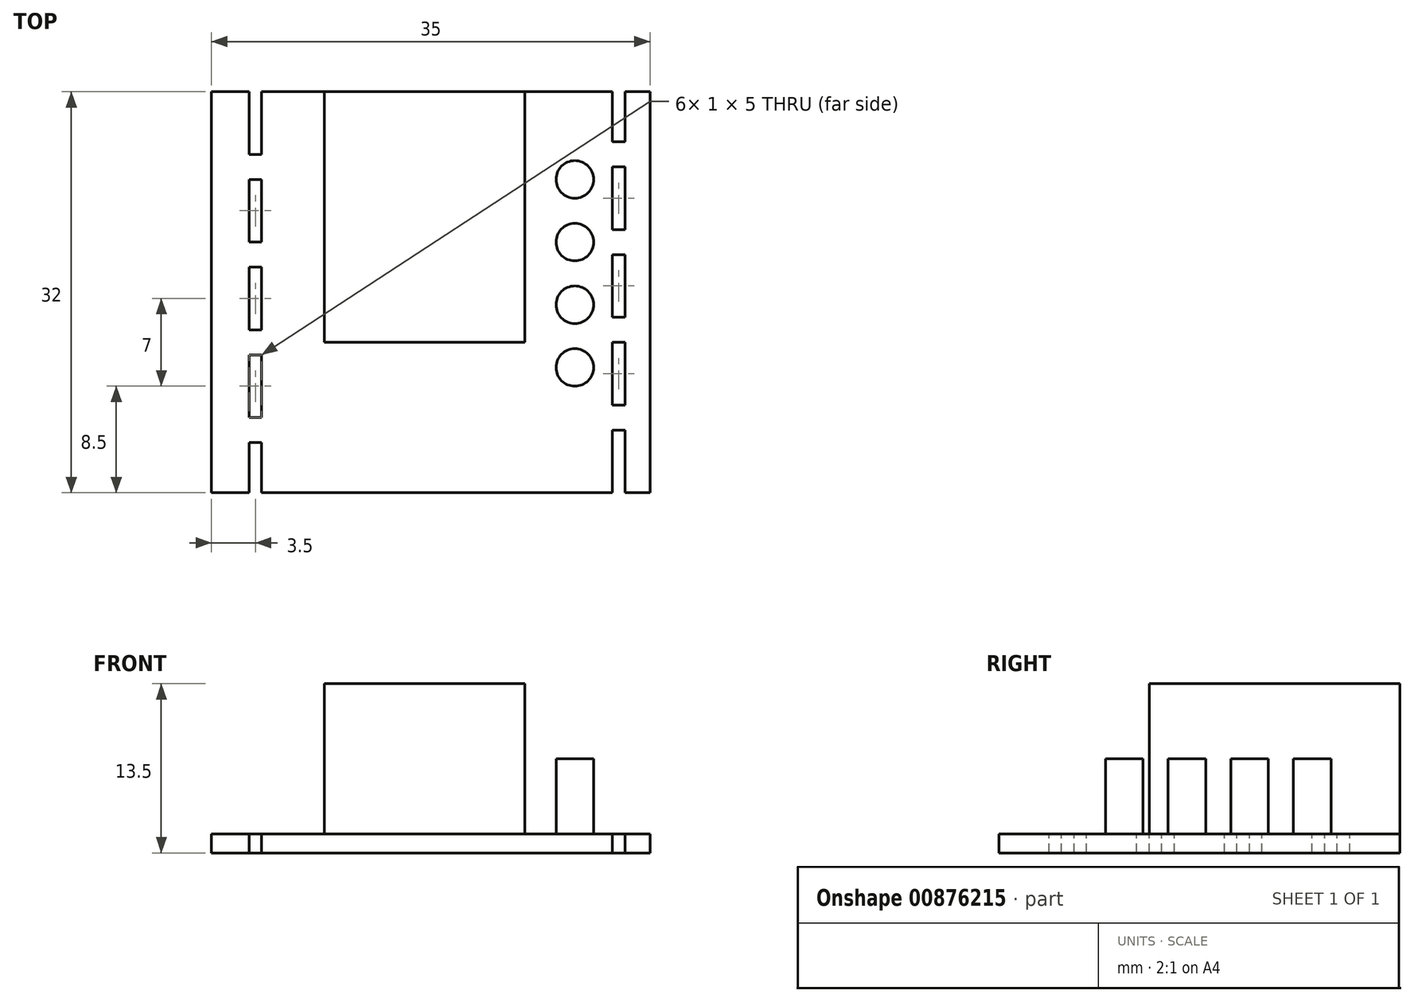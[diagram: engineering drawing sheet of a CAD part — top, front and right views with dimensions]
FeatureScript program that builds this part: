
annotation { "Feature Type Name" : "Feature", "Feature Type Description" : "" }
export const myFeature = defineFeature(function(context is Context, id is Id, definition is map)
    precondition{}
    {
        {
            var Q0;
            Q0=qCreatedBy(makeId("Top.planeOp"),FACE);
            var sketch = newSketch(context, id + "F0", { "sketchPlane" : qUnion([Q0])});
            skLineSegment(sketch, "E0.bottom", {"start": v(17.5, 16) * mm, "end": v(-17.5, 16) * mm});
            skLineSegment(sketch, "E0.top", {"start": v(17.5, -16) * mm, "end": v(-17.5, -16) * mm});
            skLineSegment(sketch, "E0.left", {"start": v(17.5, 16) * mm, "end": v(17.5, -16) * mm});
            skLineSegment(sketch, "E0.right", {"start": v(-17.5, 16) * mm, "end": v(-17.5, -16) * mm});
            skPoint(sketch, "E0.middle", {"position": v(0, 0) * mm});
            skSolve(sketch);
        }
        {
            var Q0;
            Q0=qSketchRegion(id+"F0",true);
            extrude(context, id + "F1", {"entities" : qUnion([Q0]), "depth" : 1.5 * mm, "offsetDistance" : 25 * mm});
        }
        {
            var Q0;
            Q0=makeQuery(id+"F1.opExtrude","CAP_FACE",FACE,{"disambiguationData":[OSD([sQuery(id+"F0.wireOp",EDGE,"E0.bottom"),sQuery(id+"F0.wireOp",EDGE,"E0.top"),sQuery(id+"F0.wireOp",EDGE,"E0.left"),sQuery(id+"F0.wireOp",EDGE,"E0.right")])],"isStart":false});
            var sketch = newSketch(context, id + "F2", { "sketchPlane" : qUnion([Q0])});
            skLineSegment(sketch, "E1.bottom", {"start": v(-8.5, 16) * mm, "end": v(7.5, 16) * mm});
            skLineSegment(sketch, "E1.top", {"start": v(-8.5, -4) * mm, "end": v(7.5, -4) * mm});
            skLineSegment(sketch, "E1.left", {"start": v(-8.5, 16) * mm, "end": v(-8.5, -4) * mm});
            skLineSegment(sketch, "E1.right", {"start": v(7.5, 16) * mm, "end": v(7.5, -4) * mm});
            skSolve(sketch);
        }
        {
            var Q0;
            Q0=qSketchRegion(id+"F2",true);
            extrude(context, id + "F3", {"entities" : qUnion([Q0]), "operationType" : NewBodyOperationType.ADD, "depth" : 12 * mm, "offsetDistance" : 25 * mm});
        }
        {
            var Q0;
            Q0=makeQuery(id+"F1.opExtrude","CAP_FACE",FACE,{"disambiguationData":[OSD([sQuery(id+"F0.wireOp",EDGE,"E0.bottom"),sQuery(id+"F0.wireOp",EDGE,"E0.top"),sQuery(id+"F0.wireOp",EDGE,"E0.left"),sQuery(id+"F0.wireOp",EDGE,"E0.right")])],"isStart":false});
            var sketch = newSketch(context, id + "F4", { "sketchPlane" : qUnion([Q0])});
            skCircle(sketch, "E2", {"center": v(11.5, 9) * mm, "radius": 1.5 * mm});
            skCircle(sketch, "E3.0.1.0", {"center": v(11.5, 4) * mm, "radius": 1.5 * mm});
            skCircle(sketch, "E3.0.2.0", {"center": v(11.5, -1) * mm, "radius": 1.5 * mm});
            skCircle(sketch, "E3.0.3.0", {"center": v(11.5, -6) * mm, "radius": 1.5 * mm});
            skLineSegment(sketch, "E3.direction1", {"start": v(11.5, 9) * mm, "end": v(36.5, 9) * mm, "construction": true});
            skLineSegment(sketch, "E3.direction2", {"start": v(11.5, 9) * mm, "end": v(11.5, 4) * mm, "construction": true});
            skSolve(sketch);
        }
        {
            var Q0;
            Q0=makeQuery(id+"F4.imprint","IMPRINT",FACE,{"disambiguationData":[TD([[makeQuery(id+"F4.imprint","IMPRINT",EDGE,{"derivedFrom":sQuery(id+"F4.wireOp",EDGE,"E2")}),1.0]])]});
            var Q1;
            Q1=makeQuery(id+"F4.imprint","IMPRINT",FACE,{"disambiguationData":[TD([[makeQuery(id+"F4.imprint","IMPRINT",EDGE,{"derivedFrom":sQuery(id+"F4.wireOp",EDGE,"E3.0.1.0")}),1.0]])]});
            var Q2;
            Q2=makeQuery(id+"F4.imprint","IMPRINT",FACE,{"disambiguationData":[TD([[makeQuery(id+"F4.imprint","IMPRINT",EDGE,{"derivedFrom":sQuery(id+"F4.wireOp",EDGE,"E3.0.2.0")}),1.0]])]});
            var Q3;
            Q3=makeQuery(id+"F4.imprint","IMPRINT",FACE,{"disambiguationData":[TD([[makeQuery(id+"F4.imprint","IMPRINT",EDGE,{"derivedFrom":sQuery(id+"F4.wireOp",EDGE,"E3.0.3.0")}),1.0]])]});
            extrude(context, id + "F5", {"entities" : qUnion([Q0, Q1, Q2, Q3]), "operationType" : NewBodyOperationType.ADD, "depth" : 6 * mm, "offsetDistance" : 25 * mm});
        }
        {
            var Q0;
            Q0=makeQuery(id+"F1.opExtrude","CAP_FACE",FACE,{"disambiguationData":[OSD([sQuery(id+"F0.wireOp",EDGE,"E0.bottom"),sQuery(id+"F0.wireOp",EDGE,"E0.top"),sQuery(id+"F0.wireOp",EDGE,"E0.left"),sQuery(id+"F0.wireOp",EDGE,"E0.right")])],"isStart":false});
            var sketch = newSketch(context, id + "F6", { "sketchPlane" : qUnion([Q0])});
            skLineSegment(sketch, "E4.bottom", {"start": v(-13.5, 16) * mm, "end": v(-14.5, 16) * mm});
            skLineSegment(sketch, "E4.top", {"start": v(-13.5, 11) * mm, "end": v(-14.5, 11) * mm});
            skLineSegment(sketch, "E4.left", {"start": v(-13.5, 16) * mm, "end": v(-13.5, 11) * mm});
            skLineSegment(sketch, "E4.right", {"start": v(-14.5, 16) * mm, "end": v(-14.5, 11) * mm});
            skLineSegment(sketch, "E5.0.1.0", {"start": v(-14.5, 9) * mm, "end": v(-14.5, 4) * mm});
            skLineSegment(sketch, "E5.0.1.1", {"start": v(-13.5, 4) * mm, "end": v(-14.5, 4) * mm});
            skLineSegment(sketch, "E5.0.1.2", {"start": v(-13.5, 9) * mm, "end": v(-13.5, 4) * mm});
            skLineSegment(sketch, "E5.0.1.3", {"start": v(-13.5, 9) * mm, "end": v(-14.5, 9) * mm});
            skLineSegment(sketch, "E5.0.2.0", {"start": v(-14.5, 2) * mm, "end": v(-14.5, -3) * mm});
            skLineSegment(sketch, "E5.0.2.1", {"start": v(-13.5, -3) * mm, "end": v(-14.5, -3) * mm});
            skLineSegment(sketch, "E5.0.2.2", {"start": v(-13.5, 2) * mm, "end": v(-13.5, -3) * mm});
            skLineSegment(sketch, "E5.0.2.3", {"start": v(-13.5, 2) * mm, "end": v(-14.5, 2) * mm});
            skLineSegment(sketch, "E5.0.3.0", {"start": v(-14.5, -5) * mm, "end": v(-14.5, -10) * mm});
            skLineSegment(sketch, "E5.0.3.1", {"start": v(-13.5, -10) * mm, "end": v(-14.5, -10) * mm});
            skLineSegment(sketch, "E5.0.3.2", {"start": v(-13.5, -5) * mm, "end": v(-13.5, -10) * mm});
            skLineSegment(sketch, "E5.0.3.3", {"start": v(-13.5, -5) * mm, "end": v(-14.5, -5) * mm});
            skLineSegment(sketch, "E5.0.4.0", {"start": v(-14.5, -12) * mm, "end": v(-14.5, -17) * mm});
            skLineSegment(sketch, "E5.0.4.1", {"start": v(-13.5, -17) * mm, "end": v(-14.5, -17) * mm});
            skLineSegment(sketch, "E5.0.4.2", {"start": v(-13.5, -12) * mm, "end": v(-13.5, -17) * mm});
            skLineSegment(sketch, "E5.0.4.3", {"start": v(-13.5, -12) * mm, "end": v(-14.5, -12) * mm});
            skLineSegment(sketch, "E5.direction1", {"start": v(-14.5, 11) * mm, "end": v(10.5, 11) * mm, "construction": true});
            skLineSegment(sketch, "E5.direction2", {"start": v(-14.5, 11) * mm, "end": v(-14.5, 4) * mm, "construction": true});
            skLineSegment(sketch, "E6.0.4.0", {"start": v(14.5, -11) * mm, "end": v(14.5, -16) * mm});
            skLineSegment(sketch, "E6.0.4.1", {"start": v(15.5, -16) * mm, "end": v(14.5, -16) * mm});
            skLineSegment(sketch, "E6.0.4.2", {"start": v(15.5, -11) * mm, "end": v(15.5, -16) * mm});
            skLineSegment(sketch, "E6.0.4.3", {"start": v(15.5, -11) * mm, "end": v(14.5, -11) * mm});
            skLineSegment(sketch, "E7.0.1.0", {"start": v(15.5, -4) * mm, "end": v(14.5, -4) * mm});
            skLineSegment(sketch, "E7.0.1.1", {"start": v(14.5, -4) * mm, "end": v(14.5, -9) * mm});
            skLineSegment(sketch, "E7.0.1.2", {"start": v(15.5, -4) * mm, "end": v(15.5, -9) * mm});
            skLineSegment(sketch, "E7.0.1.3", {"start": v(15.5, -9) * mm, "end": v(14.5, -9) * mm});
            skLineSegment(sketch, "E7.0.2.0", {"start": v(15.5, 3) * mm, "end": v(14.5, 3) * mm});
            skLineSegment(sketch, "E7.0.2.1", {"start": v(14.5, 3) * mm, "end": v(14.5, -2) * mm});
            skLineSegment(sketch, "E7.0.2.2", {"start": v(15.5, 3) * mm, "end": v(15.5, -2) * mm});
            skLineSegment(sketch, "E7.0.2.3", {"start": v(15.5, -2) * mm, "end": v(14.5, -2) * mm});
            skLineSegment(sketch, "E7.0.3.0", {"start": v(15.5, 10) * mm, "end": v(14.5, 10) * mm});
            skLineSegment(sketch, "E7.0.3.1", {"start": v(14.5, 10) * mm, "end": v(14.5, 5) * mm});
            skLineSegment(sketch, "E7.0.3.2", {"start": v(15.5, 10) * mm, "end": v(15.5, 5) * mm});
            skLineSegment(sketch, "E7.0.3.3", {"start": v(15.5, 5) * mm, "end": v(14.5, 5) * mm});
            skLineSegment(sketch, "E7.0.4.0", {"start": v(15.5, 17) * mm, "end": v(14.5, 17) * mm});
            skLineSegment(sketch, "E7.0.4.1", {"start": v(14.5, 17) * mm, "end": v(14.5, 12) * mm});
            skLineSegment(sketch, "E7.0.4.2", {"start": v(15.5, 17) * mm, "end": v(15.5, 12) * mm});
            skLineSegment(sketch, "E7.0.4.3", {"start": v(15.5, 12) * mm, "end": v(14.5, 12) * mm});
            skLineSegment(sketch, "E7.direction1", {"start": v(14.5, -16) * mm, "end": v(39.5, -16) * mm, "construction": true});
            skLineSegment(sketch, "E7.direction2", {"start": v(14.5, -16) * mm, "end": v(14.5, -9) * mm, "construction": true});
            skSolve(sketch);
        }
        {
            var Q0;
            Q0 = qSketchRegion(id + "F6", true);
            var Q1;
            Q1=sQuery(id+"F6.wireOp",EDGE,"E6.0.4.2");
            var Q2;
            Q2=sQuery(id+"F6.wireOp",EDGE,"E6.0.4.0");
            var Q3;
            Q3=sQuery(id+"F6.wireOp",EDGE,"E6.0.4.1");
            var Q4;
            Q4=sQuery(id+"F6.wireOp",EDGE,"E6.0.4.3");
            extrude(context, id + "F7", {"entities" : qUnion([Q0]), "operationType" : NewBodyOperationType.REMOVE, "surfaceEntities" : qUnion([Q1, Q2, Q3, Q4]), "endBound" : BoundingType.UP_TO_NEXT, "oppositeDirection" : true, "depth" : 25 * mm, "offsetDistance" : 25 * mm});
        }
    });
